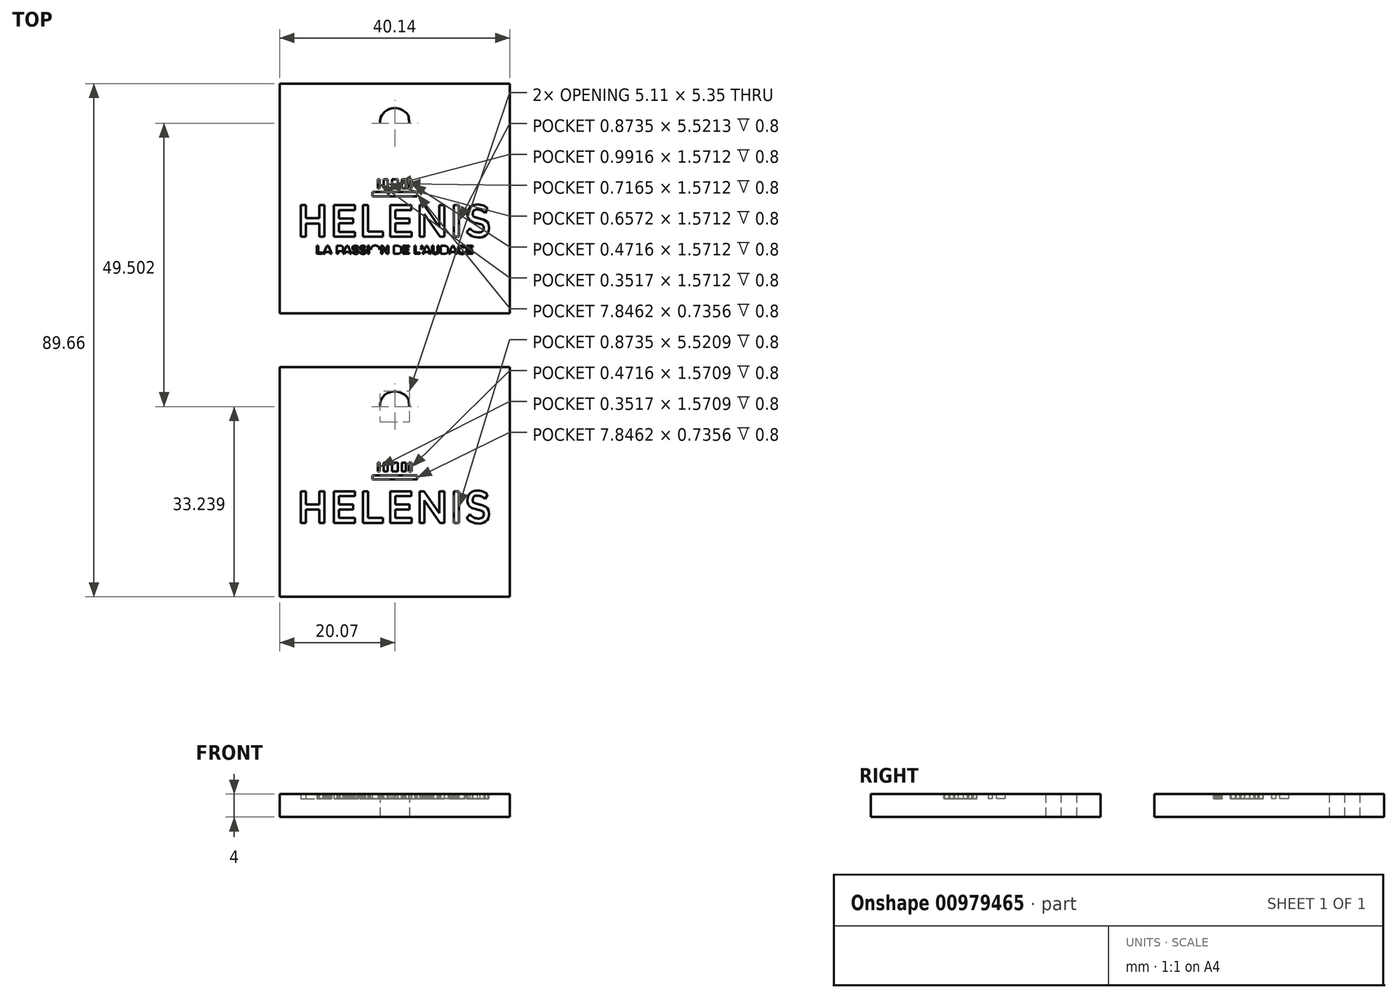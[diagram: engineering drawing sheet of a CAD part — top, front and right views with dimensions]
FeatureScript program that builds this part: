
annotation { "Feature Type Name" : "Feature", "Feature Type Description" : "" }
export const myFeature = defineFeature(function(context is Context, id is Id, definition is map)
    precondition{}
    {
        {
            var Q0;
            Q0=qCreatedBy(makeId("Top.planeOp"),FACE);
            var sketch = newSketch(context, id + "F0", { "sketchPlane" : qUnion([Q0])});
            skLineSegment(sketch, "E0", {"start": v(20.07, 44.83) * mm, "end": v(-20.07, 44.83) * mm});
            skLineSegment(sketch, "E1", {"start": v(-20.07, 44.83) * mm, "end": v(-20.07, 4.68) * mm});
            skLineSegment(sketch, "E2", {"start": v(-20.07, 4.68) * mm, "end": v(20.07, 4.68) * mm});
            skLineSegment(sketch, "E3", {"start": v(20.07, 4.68) * mm, "end": v(20.07, 44.83) * mm});
            skLineSegment(sketch, "E4", {"start": v(20.07, -4.68) * mm, "end": v(-20.07, -4.68) * mm});
            skLineSegment(sketch, "E5", {"start": v(-20.07, -4.68) * mm, "end": v(-20.07, -44.83) * mm});
            skLineSegment(sketch, "E6", {"start": v(-20.07, -44.83) * mm, "end": v(20.07, -44.83) * mm});
            skLineSegment(sketch, "E7", {"start": v(20.07, -44.83) * mm, "end": v(20.07, -4.68) * mm});
            skLineSegment(sketch, "E8", {"start": v(-13.6, 15.1) * mm, "end": v(-12.62, 15.1) * mm});
            skLineSegment(sketch, "E9", {"start": v(-12.62, 15.1) * mm, "end": v(-12.62, 15.33) * mm});
            skLineSegment(sketch, "E10", {"start": v(-12.62, 15.33) * mm, "end": v(-13.36, 15.33) * mm});
            skLineSegment(sketch, "E11", {"start": v(-13.36, 15.33) * mm, "end": v(-13.36, 16.5) * mm});
            skLineSegment(sketch, "E12", {"start": v(-13.36, 16.5) * mm, "end": v(-13.6, 16.5) * mm});
            skLineSegment(sketch, "E13", {"start": v(-13.6, 16.5) * mm, "end": v(-13.6, 15.1) * mm});
            skLineSegment(sketch, "E14", {"start": v(-11.62, 16.52) * mm, "end": v(-11.85, 16.52) * mm});
            skLineSegment(sketch, "E15", {"start": v(-11.85, 16.52) * mm, "end": v(-12.46, 15.1) * mm});
            skLineSegment(sketch, "E16", {"start": v(-12.46, 15.1) * mm, "end": v(-12.21, 15.1) * mm});
            skLineSegment(sketch, "E17", {"start": v(-12.21, 15.1) * mm, "end": v(-12.07, 15.44) * mm});
            skLineSegment(sketch, "E18", {"start": v(-12.07, 15.44) * mm, "end": v(-11.4, 15.44) * mm});
            skLineSegment(sketch, "E19", {"start": v(-11.4, 15.44) * mm, "end": v(-11.26, 15.1) * mm});
            skLineSegment(sketch, "E20", {"start": v(-11.26, 15.1) * mm, "end": v(-11, 15.1) * mm});
            skLineSegment(sketch, "E21", {"start": v(-11, 15.1) * mm, "end": v(-11.62, 16.52) * mm});
            skLineSegment(sketch, "E22", {"start": v(-11.5, 15.66) * mm, "end": v(-11.98, 15.66) * mm});
            skLineSegment(sketch, "E23", {"start": v(-11.98, 15.66) * mm, "end": v(-11.74, 16.22) * mm});
            skLineSegment(sketch, "E24", {"start": v(-11.74, 16.22) * mm, "end": v(-11.5, 15.66) * mm});
            skLineSegment(sketch, "E25", {"start": v(-9.57, 16.5) * mm, "end": v(-10.12, 16.5) * mm});
            skLineSegment(sketch, "E26", {"start": v(-10.12, 16.5) * mm, "end": v(-10.12, 15.1) * mm});
            skLineSegment(sketch, "E27", {"start": v(-10.12, 15.1) * mm, "end": v(-9.87, 15.1) * mm});
            skLineSegment(sketch, "E28", {"start": v(-9.87, 15.1) * mm, "end": v(-9.87, 15.56) * mm});
            skLineSegment(sketch, "E29", {"start": v(-9.87, 15.56) * mm, "end": v(-9.6, 15.56) * mm});
            skLineSegment(sketch, "E30", {"start": v(-9.59, 15.78) * mm, "end": v(-9.87, 15.78) * mm});
            skLineSegment(sketch, "E31", {"start": v(-9.87, 15.78) * mm, "end": v(-9.87, 16.28) * mm});
            skLineSegment(sketch, "E32", {"start": v(-9.87, 16.28) * mm, "end": v(-9.59, 16.28) * mm});
            skLineSegment(sketch, "E33", {"start": v(-8.18, 16.52) * mm, "end": v(-8.4, 16.52) * mm});
            skLineSegment(sketch, "E34", {"start": v(-8.4, 16.52) * mm, "end": v(-9.02, 15.1) * mm});
            skLineSegment(sketch, "E35", {"start": v(-9.02, 15.1) * mm, "end": v(-8.77, 15.1) * mm});
            skLineSegment(sketch, "E36", {"start": v(-8.77, 15.1) * mm, "end": v(-8.63, 15.44) * mm});
            skLineSegment(sketch, "E37", {"start": v(-8.63, 15.44) * mm, "end": v(-7.96, 15.44) * mm});
            skLineSegment(sketch, "E38", {"start": v(-7.96, 15.44) * mm, "end": v(-7.82, 15.1) * mm});
            skLineSegment(sketch, "E39", {"start": v(-7.82, 15.1) * mm, "end": v(-7.56, 15.1) * mm});
            skLineSegment(sketch, "E40", {"start": v(-7.56, 15.1) * mm, "end": v(-8.18, 16.52) * mm});
            skLineSegment(sketch, "E41", {"start": v(-8.05, 15.66) * mm, "end": v(-8.54, 15.66) * mm});
            skLineSegment(sketch, "E42", {"start": v(-8.54, 15.66) * mm, "end": v(-8.3, 16.22) * mm});
            skLineSegment(sketch, "E43", {"start": v(-8.3, 16.22) * mm, "end": v(-8.05, 15.66) * mm});
            skLineSegment(sketch, "E44", {"start": v(-6.5, 16.16) * mm, "end": v(-6.37, 16.35) * mm});
            skLineSegment(sketch, "E45", {"start": v(-7.27, 15.49) * mm, "end": v(-7.42, 15.3) * mm});
            skLineSegment(sketch, "E46", {"start": v(-5.23, 16.16) * mm, "end": v(-5.1, 16.35) * mm});
            skLineSegment(sketch, "E47", {"start": v(-5.99, 15.49) * mm, "end": v(-6.14, 15.3) * mm});
            skLineSegment(sketch, "E48", {"start": v(-4.73, 15.1) * mm, "end": v(-4.48, 15.1) * mm});
            skLineSegment(sketch, "E49", {"start": v(-4.48, 15.1) * mm, "end": v(-4.48, 16.5) * mm});
            skLineSegment(sketch, "E50", {"start": v(-4.48, 16.5) * mm, "end": v(-4.73, 16.5) * mm});
            skLineSegment(sketch, "E51", {"start": v(-4.73, 16.5) * mm, "end": v(-4.73, 15.1) * mm});
            skLineSegment(sketch, "E52", {"start": v(-1.39, 15.54) * mm, "end": v(-2.14, 16.5) * mm});
            skLineSegment(sketch, "E53", {"start": v(-2.14, 16.5) * mm, "end": v(-2.36, 16.5) * mm});
            skLineSegment(sketch, "E54", {"start": v(-2.36, 16.5) * mm, "end": v(-2.36, 15.1) * mm});
            skLineSegment(sketch, "E55", {"start": v(-2.36, 15.1) * mm, "end": v(-2.12, 15.1) * mm});
            skLineSegment(sketch, "E56", {"start": v(-2.12, 15.1) * mm, "end": v(-2.12, 16.1) * mm});
            skLineSegment(sketch, "E57", {"start": v(-2.12, 16.1) * mm, "end": v(-1.35, 15.1) * mm});
            skLineSegment(sketch, "E58", {"start": v(-1.35, 15.1) * mm, "end": v(-1.14, 15.1) * mm});
            skLineSegment(sketch, "E59", {"start": v(-1.14, 15.1) * mm, "end": v(-1.14, 16.5) * mm});
            skLineSegment(sketch, "E60", {"start": v(-1.14, 16.5) * mm, "end": v(-1.39, 16.5) * mm});
            skLineSegment(sketch, "E61", {"start": v(-1.39, 16.5) * mm, "end": v(-1.39, 15.54) * mm});
            skLineSegment(sketch, "E62", {"start": v(0.38, 16.5) * mm, "end": v(-0.14, 16.5) * mm});
            skLineSegment(sketch, "E63", {"start": v(-0.14, 16.5) * mm, "end": v(-0.14, 15.1) * mm});
            skLineSegment(sketch, "E64", {"start": v(-0.14, 15.1) * mm, "end": v(0.38, 15.1) * mm});
            skLineSegment(sketch, "E65", {"start": v(0.38, 15.33) * mm, "end": v(0.1, 15.33) * mm});
            skLineSegment(sketch, "E66", {"start": v(0.1, 15.33) * mm, "end": v(0.1, 16.28) * mm});
            skLineSegment(sketch, "E67", {"start": v(0.1, 16.28) * mm, "end": v(0.38, 16.28) * mm});
            skLineSegment(sketch, "E68", {"start": v(2.48, 16.5) * mm, "end": v(1.44, 16.5) * mm});
            skLineSegment(sketch, "E69", {"start": v(1.44, 16.5) * mm, "end": v(1.44, 15.1) * mm});
            skLineSegment(sketch, "E70", {"start": v(1.44, 15.1) * mm, "end": v(2.5, 15.1) * mm});
            skLineSegment(sketch, "E71", {"start": v(2.5, 15.1) * mm, "end": v(2.5, 15.33) * mm});
            skLineSegment(sketch, "E72", {"start": v(2.5, 15.33) * mm, "end": v(1.7, 15.33) * mm});
            skLineSegment(sketch, "E73", {"start": v(1.7, 15.33) * mm, "end": v(1.7, 15.7) * mm});
            skLineSegment(sketch, "E74", {"start": v(1.7, 15.7) * mm, "end": v(2.4, 15.7) * mm});
            skLineSegment(sketch, "E75", {"start": v(2.4, 15.7) * mm, "end": v(2.4, 15.92) * mm});
            skLineSegment(sketch, "E76", {"start": v(2.4, 15.92) * mm, "end": v(1.7, 15.92) * mm});
            skLineSegment(sketch, "E77", {"start": v(1.7, 15.92) * mm, "end": v(1.7, 16.29) * mm});
            skLineSegment(sketch, "E78", {"start": v(1.7, 16.29) * mm, "end": v(2.48, 16.29) * mm});
            skLineSegment(sketch, "E79", {"start": v(2.48, 16.29) * mm, "end": v(2.48, 16.5) * mm});
            skLineSegment(sketch, "E80", {"start": v(3.43, 15.1) * mm, "end": v(4.4, 15.1) * mm});
            skLineSegment(sketch, "E81", {"start": v(4.4, 15.1) * mm, "end": v(4.4, 15.33) * mm});
            skLineSegment(sketch, "E82", {"start": v(4.4, 15.33) * mm, "end": v(3.67, 15.33) * mm});
            skLineSegment(sketch, "E83", {"start": v(3.67, 15.33) * mm, "end": v(3.67, 16.5) * mm});
            skLineSegment(sketch, "E84", {"start": v(3.67, 16.5) * mm, "end": v(3.43, 16.5) * mm});
            skLineSegment(sketch, "E85", {"start": v(3.43, 16.5) * mm, "end": v(3.43, 15.1) * mm});
            skLineSegment(sketch, "E86", {"start": v(4.5, 16.04) * mm, "end": v(4.53, 15.94) * mm});
            skLineSegment(sketch, "E87", {"start": v(4.84, 16.27) * mm, "end": v(4.84, 16.5) * mm});
            skLineSegment(sketch, "E88", {"start": v(4.84, 16.5) * mm, "end": v(4.57, 16.5) * mm});
            skLineSegment(sketch, "E89", {"start": v(4.57, 16.5) * mm, "end": v(4.57, 16.23) * mm});
            skLineSegment(sketch, "E90", {"start": v(4.57, 16.23) * mm, "end": v(4.67, 16.23) * mm});
            skLineSegment(sketch, "E91", {"start": v(5.69, 16.52) * mm, "end": v(5.46, 16.52) * mm});
            skLineSegment(sketch, "E92", {"start": v(5.46, 16.52) * mm, "end": v(4.84, 15.1) * mm});
            skLineSegment(sketch, "E93", {"start": v(4.84, 15.1) * mm, "end": v(5.1, 15.1) * mm});
            skLineSegment(sketch, "E94", {"start": v(5.1, 15.1) * mm, "end": v(5.24, 15.44) * mm});
            skLineSegment(sketch, "E95", {"start": v(5.24, 15.44) * mm, "end": v(5.9, 15.44) * mm});
            skLineSegment(sketch, "E96", {"start": v(5.9, 15.44) * mm, "end": v(6.04, 15.1) * mm});
            skLineSegment(sketch, "E97", {"start": v(6.04, 15.1) * mm, "end": v(6.3, 15.1) * mm});
            skLineSegment(sketch, "E98", {"start": v(6.3, 15.1) * mm, "end": v(5.69, 16.52) * mm});
            skLineSegment(sketch, "E99", {"start": v(5.81, 15.66) * mm, "end": v(5.33, 15.66) * mm});
            skLineSegment(sketch, "E100", {"start": v(5.33, 15.66) * mm, "end": v(5.57, 16.22) * mm});
            skLineSegment(sketch, "E101", {"start": v(5.57, 16.22) * mm, "end": v(5.81, 15.66) * mm});
            skLineSegment(sketch, "E102", {"start": v(7.7, 16.5) * mm, "end": v(7.45, 16.5) * mm});
            skLineSegment(sketch, "E103", {"start": v(7.45, 16.5) * mm, "end": v(7.45, 15.7) * mm});
            skLineSegment(sketch, "E104", {"start": v(6.74, 15.7) * mm, "end": v(6.74, 16.5) * mm});
            skLineSegment(sketch, "E105", {"start": v(6.74, 16.5) * mm, "end": v(6.5, 16.5) * mm});
            skLineSegment(sketch, "E106", {"start": v(6.5, 16.5) * mm, "end": v(6.5, 15.7) * mm});
            skLineSegment(sketch, "E107", {"start": v(7.7, 15.71) * mm, "end": v(7.7, 16.5) * mm});
            skLineSegment(sketch, "E108", {"start": v(8.57, 16.5) * mm, "end": v(8.05, 16.5) * mm});
            skLineSegment(sketch, "E109", {"start": v(8.05, 16.5) * mm, "end": v(8.05, 15.1) * mm});
            skLineSegment(sketch, "E110", {"start": v(8.05, 15.1) * mm, "end": v(8.57, 15.1) * mm});
            skLineSegment(sketch, "E111", {"start": v(8.57, 15.33) * mm, "end": v(8.3, 15.33) * mm});
            skLineSegment(sketch, "E112", {"start": v(8.3, 15.33) * mm, "end": v(8.3, 16.28) * mm});
            skLineSegment(sketch, "E113", {"start": v(8.3, 16.28) * mm, "end": v(8.57, 16.28) * mm});
            skLineSegment(sketch, "E114", {"start": v(10.26, 16.52) * mm, "end": v(10.04, 16.52) * mm});
            skLineSegment(sketch, "E115", {"start": v(10.04, 16.52) * mm, "end": v(9.42, 15.1) * mm});
            skLineSegment(sketch, "E116", {"start": v(9.42, 15.1) * mm, "end": v(9.67, 15.1) * mm});
            skLineSegment(sketch, "E117", {"start": v(9.67, 15.1) * mm, "end": v(9.82, 15.44) * mm});
            skLineSegment(sketch, "E118", {"start": v(9.82, 15.44) * mm, "end": v(10.48, 15.44) * mm});
            skLineSegment(sketch, "E119", {"start": v(10.48, 15.44) * mm, "end": v(10.62, 15.1) * mm});
            skLineSegment(sketch, "E120", {"start": v(10.62, 15.1) * mm, "end": v(10.88, 15.1) * mm});
            skLineSegment(sketch, "E121", {"start": v(10.88, 15.1) * mm, "end": v(10.26, 16.52) * mm});
            skLineSegment(sketch, "E122", {"start": v(10.39, 15.66) * mm, "end": v(9.9, 15.66) * mm});
            skLineSegment(sketch, "E123", {"start": v(9.9, 15.66) * mm, "end": v(10.15, 16.22) * mm});
            skLineSegment(sketch, "E124", {"start": v(10.15, 16.22) * mm, "end": v(10.39, 15.66) * mm});
            skLineSegment(sketch, "E125", {"start": v(12.27, 15.33) * mm, "end": v(12.12, 15.49) * mm});
            skLineSegment(sketch, "E126", {"start": v(12.1, 16.13) * mm, "end": v(12.26, 16.31) * mm});
            skLineSegment(sketch, "E127", {"start": v(13.6, 16.5) * mm, "end": v(12.55, 16.5) * mm});
            skLineSegment(sketch, "E128", {"start": v(12.55, 16.5) * mm, "end": v(12.55, 15.1) * mm});
            skLineSegment(sketch, "E129", {"start": v(12.55, 15.1) * mm, "end": v(13.6, 15.1) * mm});
            skLineSegment(sketch, "E130", {"start": v(13.6, 15.1) * mm, "end": v(13.6, 15.33) * mm});
            skLineSegment(sketch, "E131", {"start": v(13.6, 15.33) * mm, "end": v(12.8, 15.33) * mm});
            skLineSegment(sketch, "E132", {"start": v(12.8, 15.33) * mm, "end": v(12.8, 15.7) * mm});
            skLineSegment(sketch, "E133", {"start": v(12.8, 15.7) * mm, "end": v(13.5, 15.7) * mm});
            skLineSegment(sketch, "E134", {"start": v(13.5, 15.7) * mm, "end": v(13.5, 15.92) * mm});
            skLineSegment(sketch, "E135", {"start": v(13.5, 15.92) * mm, "end": v(12.8, 15.92) * mm});
            skLineSegment(sketch, "E136", {"start": v(12.8, 15.92) * mm, "end": v(12.8, 16.29) * mm});
            skLineSegment(sketch, "E137", {"start": v(12.8, 16.29) * mm, "end": v(13.6, 16.29) * mm});
            skLineSegment(sketch, "E138", {"start": v(13.6, 16.29) * mm, "end": v(13.6, 16.5) * mm});
            skLineSegment(sketch, "E139", {"start": v(-3.92, 25.17) * mm, "end": v(3.92, 25.17) * mm});
            skLineSegment(sketch, "E140", {"start": v(3.92, 25.17) * mm, "end": v(3.92, 25.9) * mm});
            skLineSegment(sketch, "E141", {"start": v(3.92, 25.9) * mm, "end": v(-3.92, 25.9) * mm});
            skLineSegment(sketch, "E142", {"start": v(-3.92, 25.9) * mm, "end": v(-3.92, 25.17) * mm});
            skLineSegment(sketch, "E143", {"start": v(-2.97, 26.56) * mm, "end": v(-2.62, 26.56) * mm});
            skLineSegment(sketch, "E144", {"start": v(-2.62, 26.56) * mm, "end": v(-2.62, 28.13) * mm});
            skLineSegment(sketch, "E145", {"start": v(-2.62, 28.13) * mm, "end": v(-2.97, 28.13) * mm});
            skLineSegment(sketch, "E146", {"start": v(-2.97, 28.13) * mm, "end": v(-2.97, 26.56) * mm});
            skLineSegment(sketch, "E147", {"start": v(2.47, 26.56) * mm, "end": v(2.94, 26.56) * mm});
            skLineSegment(sketch, "E148", {"start": v(2.94, 26.56) * mm, "end": v(2.94, 28.13) * mm});
            skLineSegment(sketch, "E149", {"start": v(2.94, 28.13) * mm, "end": v(2.47, 28.13) * mm});
            skLineSegment(sketch, "E150", {"start": v(2.47, 28.13) * mm, "end": v(2.47, 26.56) * mm});
            skLineSegment(sketch, "E151", {"start": v(-1.93, 26.56) * mm, "end": v(-1.27, 26.56) * mm});
            skLineSegment(sketch, "E152", {"start": v(-1.27, 26.56) * mm, "end": v(-1.27, 28.13) * mm});
            skLineSegment(sketch, "E153", {"start": v(-1.27, 28.13) * mm, "end": v(-1.93, 28.13) * mm});
            skLineSegment(sketch, "E154", {"start": v(-1.93, 28.13) * mm, "end": v(-1.93, 26.56) * mm});
            skLineSegment(sketch, "E155", {"start": v(1.23, 26.56) * mm, "end": v(1.95, 26.56) * mm});
            skLineSegment(sketch, "E156", {"start": v(1.95, 26.56) * mm, "end": v(1.95, 28.13) * mm});
            skLineSegment(sketch, "E157", {"start": v(1.95, 28.13) * mm, "end": v(1.23, 28.13) * mm});
            skLineSegment(sketch, "E158", {"start": v(1.23, 28.13) * mm, "end": v(1.23, 26.56) * mm});
            skLineSegment(sketch, "E159", {"start": v(-0.47, 26.56) * mm, "end": v(0.52, 26.56) * mm});
            skLineSegment(sketch, "E160", {"start": v(0.52, 26.56) * mm, "end": v(0.52, 28.13) * mm});
            skLineSegment(sketch, "E161", {"start": v(0.52, 28.13) * mm, "end": v(-0.47, 28.13) * mm});
            skLineSegment(sketch, "E162", {"start": v(-0.47, 28.13) * mm, "end": v(-0.47, 26.56) * mm});
            skLineSegment(sketch, "E163", {"start": v(-13.16, 20.41) * mm, "end": v(-13.16, 18.09) * mm});
            skLineSegment(sketch, "E164", {"start": v(-13.16, 18.09) * mm, "end": v(-12.28, 18.09) * mm});
            skLineSegment(sketch, "E165", {"start": v(-12.28, 18.09) * mm, "end": v(-12.28, 23.6) * mm});
            skLineSegment(sketch, "E166", {"start": v(-12.28, 23.6) * mm, "end": v(-13.16, 23.6) * mm});
            skLineSegment(sketch, "E167", {"start": v(-13.16, 23.6) * mm, "end": v(-13.16, 21.31) * mm});
            skLineSegment(sketch, "E168", {"start": v(-13.16, 21.31) * mm, "end": v(-15.53, 21.31) * mm});
            skLineSegment(sketch, "E169", {"start": v(-15.53, 21.31) * mm, "end": v(-15.53, 23.6) * mm});
            skLineSegment(sketch, "E170", {"start": v(-15.53, 23.6) * mm, "end": v(-16.4, 23.6) * mm});
            skLineSegment(sketch, "E171", {"start": v(-16.4, 23.6) * mm, "end": v(-16.4, 18.09) * mm});
            skLineSegment(sketch, "E172", {"start": v(-16.4, 18.09) * mm, "end": v(-15.53, 18.09) * mm});
            skLineSegment(sketch, "E173", {"start": v(-15.53, 18.09) * mm, "end": v(-15.53, 20.41) * mm});
            skLineSegment(sketch, "E174", {"start": v(-15.53, 20.41) * mm, "end": v(-13.16, 20.41) * mm});
            skLineSegment(sketch, "E175", {"start": v(-6.97, 23.6) * mm, "end": v(-10.65, 23.6) * mm});
            skLineSegment(sketch, "E176", {"start": v(-10.65, 23.6) * mm, "end": v(-10.65, 18.09) * mm});
            skLineSegment(sketch, "E177", {"start": v(-10.65, 18.09) * mm, "end": v(-6.93, 18.09) * mm});
            skLineSegment(sketch, "E178", {"start": v(-6.93, 18.09) * mm, "end": v(-6.93, 18.96) * mm});
            skLineSegment(sketch, "E179", {"start": v(-6.93, 18.96) * mm, "end": v(-9.78, 18.96) * mm});
            skLineSegment(sketch, "E180", {"start": v(-9.78, 18.96) * mm, "end": v(-9.78, 20.44) * mm});
            skLineSegment(sketch, "E181", {"start": v(-9.78, 20.44) * mm, "end": v(-7.29, 20.44) * mm});
            skLineSegment(sketch, "E182", {"start": v(-7.29, 20.44) * mm, "end": v(-7.29, 21.3) * mm});
            skLineSegment(sketch, "E183", {"start": v(-7.29, 21.3) * mm, "end": v(-9.78, 21.3) * mm});
            skLineSegment(sketch, "E184", {"start": v(-9.78, 21.3) * mm, "end": v(-9.78, 22.74) * mm});
            skLineSegment(sketch, "E185", {"start": v(-9.78, 22.74) * mm, "end": v(-6.97, 22.74) * mm});
            skLineSegment(sketch, "E186", {"start": v(-6.97, 22.74) * mm, "end": v(-6.97, 23.6) * mm});
            skLineSegment(sketch, "E187", {"start": v(-5.54, 18.09) * mm, "end": v(-2.05, 18.09) * mm});
            skLineSegment(sketch, "E188", {"start": v(-2.05, 18.09) * mm, "end": v(-2.05, 18.97) * mm});
            skLineSegment(sketch, "E189", {"start": v(-2.05, 18.97) * mm, "end": v(-4.67, 18.97) * mm});
            skLineSegment(sketch, "E190", {"start": v(-4.67, 18.97) * mm, "end": v(-4.67, 23.6) * mm});
            skLineSegment(sketch, "E191", {"start": v(-4.67, 23.6) * mm, "end": v(-5.54, 23.6) * mm});
            skLineSegment(sketch, "E192", {"start": v(-5.54, 23.6) * mm, "end": v(-5.54, 18.09) * mm});
            skLineSegment(sketch, "E193", {"start": v(2.9, 23.6) * mm, "end": v(-0.8, 23.6) * mm});
            skLineSegment(sketch, "E194", {"start": v(-0.8, 23.6) * mm, "end": v(-0.8, 18.09) * mm});
            skLineSegment(sketch, "E195", {"start": v(-0.8, 18.09) * mm, "end": v(2.93, 18.09) * mm});
            skLineSegment(sketch, "E196", {"start": v(2.93, 18.09) * mm, "end": v(2.93, 18.96) * mm});
            skLineSegment(sketch, "E197", {"start": v(2.93, 18.96) * mm, "end": v(0.08, 18.96) * mm});
            skLineSegment(sketch, "E198", {"start": v(0.08, 18.96) * mm, "end": v(0.08, 20.44) * mm});
            skLineSegment(sketch, "E199", {"start": v(0.08, 20.44) * mm, "end": v(2.57, 20.44) * mm});
            skLineSegment(sketch, "E200", {"start": v(2.57, 20.44) * mm, "end": v(2.57, 21.3) * mm});
            skLineSegment(sketch, "E201", {"start": v(2.57, 21.3) * mm, "end": v(0.08, 21.3) * mm});
            skLineSegment(sketch, "E202", {"start": v(0.08, 21.3) * mm, "end": v(0.08, 22.74) * mm});
            skLineSegment(sketch, "E203", {"start": v(0.08, 22.74) * mm, "end": v(2.9, 22.74) * mm});
            skLineSegment(sketch, "E204", {"start": v(2.9, 22.74) * mm, "end": v(2.9, 23.6) * mm});
            skLineSegment(sketch, "E205", {"start": v(7.8, 19.8) * mm, "end": v(5.13, 23.6) * mm});
            skLineSegment(sketch, "E206", {"start": v(5.13, 23.6) * mm, "end": v(4.32, 23.6) * mm});
            skLineSegment(sketch, "E207", {"start": v(4.32, 23.6) * mm, "end": v(4.32, 18.09) * mm});
            skLineSegment(sketch, "E208", {"start": v(4.32, 18.09) * mm, "end": v(5.18, 18.09) * mm});
            skLineSegment(sketch, "E209", {"start": v(5.18, 18.09) * mm, "end": v(5.18, 22.02) * mm});
            skLineSegment(sketch, "E210", {"start": v(5.18, 22.02) * mm, "end": v(7.92, 18.09) * mm});
            skLineSegment(sketch, "E211", {"start": v(7.92, 18.09) * mm, "end": v(8.65, 18.09) * mm});
            skLineSegment(sketch, "E212", {"start": v(8.65, 18.09) * mm, "end": v(8.65, 23.6) * mm});
            skLineSegment(sketch, "E213", {"start": v(8.65, 23.6) * mm, "end": v(7.8, 23.6) * mm});
            skLineSegment(sketch, "E214", {"start": v(7.8, 23.6) * mm, "end": v(7.8, 19.8) * mm});
            skLineSegment(sketch, "E215", {"start": v(10.33, 18.09) * mm, "end": v(11.2, 18.09) * mm});
            skLineSegment(sketch, "E216", {"start": v(11.2, 18.09) * mm, "end": v(11.2, 23.6) * mm});
            skLineSegment(sketch, "E217", {"start": v(11.2, 23.6) * mm, "end": v(10.33, 23.6) * mm});
            skLineSegment(sketch, "E218", {"start": v(10.33, 23.6) * mm, "end": v(10.33, 18.09) * mm});
            skLineSegment(sketch, "E219", {"start": v(15.78, 22.26) * mm, "end": v(16.25, 23) * mm});
            skLineSegment(sketch, "E220", {"start": v(13.08, 19.59) * mm, "end": v(12.55, 18.9) * mm});
            skLineSegment(sketch, "E221", {"start": v(-3.92, -24.34) * mm, "end": v(3.92, -24.34) * mm});
            skLineSegment(sketch, "E222", {"start": v(3.92, -24.34) * mm, "end": v(3.92, -23.6) * mm});
            skLineSegment(sketch, "E223", {"start": v(3.92, -23.6) * mm, "end": v(-3.92, -23.6) * mm});
            skLineSegment(sketch, "E224", {"start": v(-3.92, -23.6) * mm, "end": v(-3.92, -24.34) * mm});
            skLineSegment(sketch, "E225", {"start": v(-2.97, -22.94) * mm, "end": v(-2.62, -22.94) * mm});
            skLineSegment(sketch, "E226", {"start": v(-2.62, -22.94) * mm, "end": v(-2.62, -21.37) * mm});
            skLineSegment(sketch, "E227", {"start": v(-2.62, -21.37) * mm, "end": v(-2.97, -21.37) * mm});
            skLineSegment(sketch, "E228", {"start": v(-2.97, -21.37) * mm, "end": v(-2.97, -22.94) * mm});
            skLineSegment(sketch, "E229", {"start": v(2.47, -22.94) * mm, "end": v(2.94, -22.94) * mm});
            skLineSegment(sketch, "E230", {"start": v(2.94, -22.94) * mm, "end": v(2.94, -21.37) * mm});
            skLineSegment(sketch, "E231", {"start": v(2.94, -21.37) * mm, "end": v(2.47, -21.37) * mm});
            skLineSegment(sketch, "E232", {"start": v(2.47, -21.37) * mm, "end": v(2.47, -22.94) * mm});
            skLineSegment(sketch, "E233", {"start": v(-1.93, -22.94) * mm, "end": v(-1.27, -22.94) * mm});
            skLineSegment(sketch, "E234", {"start": v(-1.27, -22.94) * mm, "end": v(-1.27, -21.37) * mm});
            skLineSegment(sketch, "E235", {"start": v(-1.27, -21.37) * mm, "end": v(-1.93, -21.37) * mm});
            skLineSegment(sketch, "E236", {"start": v(-1.93, -21.37) * mm, "end": v(-1.93, -22.94) * mm});
            skLineSegment(sketch, "E237", {"start": v(1.23, -22.94) * mm, "end": v(1.95, -22.94) * mm});
            skLineSegment(sketch, "E238", {"start": v(1.95, -22.94) * mm, "end": v(1.95, -21.37) * mm});
            skLineSegment(sketch, "E239", {"start": v(1.95, -21.37) * mm, "end": v(1.23, -21.37) * mm});
            skLineSegment(sketch, "E240", {"start": v(1.23, -21.37) * mm, "end": v(1.23, -22.94) * mm});
            skLineSegment(sketch, "E241", {"start": v(-0.47, -22.94) * mm, "end": v(0.52, -22.94) * mm});
            skLineSegment(sketch, "E242", {"start": v(0.52, -22.94) * mm, "end": v(0.52, -21.37) * mm});
            skLineSegment(sketch, "E243", {"start": v(0.52, -21.37) * mm, "end": v(-0.47, -21.37) * mm});
            skLineSegment(sketch, "E244", {"start": v(-0.47, -21.37) * mm, "end": v(-0.47, -22.94) * mm});
            skLineSegment(sketch, "E245", {"start": v(-13.16, -29.59) * mm, "end": v(-13.16, -31.92) * mm});
            skLineSegment(sketch, "E246", {"start": v(-13.16, -31.92) * mm, "end": v(-12.28, -31.92) * mm});
            skLineSegment(sketch, "E247", {"start": v(-12.28, -31.92) * mm, "end": v(-12.28, -26.4) * mm});
            skLineSegment(sketch, "E248", {"start": v(-12.28, -26.4) * mm, "end": v(-13.16, -26.4) * mm});
            skLineSegment(sketch, "E249", {"start": v(-13.16, -26.4) * mm, "end": v(-13.16, -28.69) * mm});
            skLineSegment(sketch, "E250", {"start": v(-13.16, -28.69) * mm, "end": v(-15.53, -28.69) * mm});
            skLineSegment(sketch, "E251", {"start": v(-15.53, -28.69) * mm, "end": v(-15.53, -26.4) * mm});
            skLineSegment(sketch, "E252", {"start": v(-15.53, -26.4) * mm, "end": v(-16.4, -26.4) * mm});
            skLineSegment(sketch, "E253", {"start": v(-16.4, -26.4) * mm, "end": v(-16.4, -31.92) * mm});
            skLineSegment(sketch, "E254", {"start": v(-16.4, -31.92) * mm, "end": v(-15.53, -31.92) * mm});
            skLineSegment(sketch, "E255", {"start": v(-15.53, -31.92) * mm, "end": v(-15.53, -29.59) * mm});
            skLineSegment(sketch, "E256", {"start": v(-15.53, -29.59) * mm, "end": v(-13.16, -29.59) * mm});
            skLineSegment(sketch, "E257", {"start": v(-6.97, -26.4) * mm, "end": v(-10.65, -26.4) * mm});
            skLineSegment(sketch, "E258", {"start": v(-10.65, -26.4) * mm, "end": v(-10.65, -31.92) * mm});
            skLineSegment(sketch, "E259", {"start": v(-10.65, -31.92) * mm, "end": v(-6.93, -31.92) * mm});
            skLineSegment(sketch, "E260", {"start": v(-6.93, -31.92) * mm, "end": v(-6.93, -31.05) * mm});
            skLineSegment(sketch, "E261", {"start": v(-6.93, -31.05) * mm, "end": v(-9.78, -31.05) * mm});
            skLineSegment(sketch, "E262", {"start": v(-9.78, -31.05) * mm, "end": v(-9.78, -29.56) * mm});
            skLineSegment(sketch, "E263", {"start": v(-9.78, -29.56) * mm, "end": v(-7.29, -29.56) * mm});
            skLineSegment(sketch, "E264", {"start": v(-7.29, -29.56) * mm, "end": v(-7.29, -28.7) * mm});
            skLineSegment(sketch, "E265", {"start": v(-7.29, -28.7) * mm, "end": v(-9.78, -28.7) * mm});
            skLineSegment(sketch, "E266", {"start": v(-9.78, -28.7) * mm, "end": v(-9.78, -27.26) * mm});
            skLineSegment(sketch, "E267", {"start": v(-9.78, -27.26) * mm, "end": v(-6.97, -27.26) * mm});
            skLineSegment(sketch, "E268", {"start": v(-6.97, -27.26) * mm, "end": v(-6.97, -26.4) * mm});
            skLineSegment(sketch, "E269", {"start": v(-5.54, -31.92) * mm, "end": v(-2.05, -31.92) * mm});
            skLineSegment(sketch, "E270", {"start": v(-2.05, -31.92) * mm, "end": v(-2.05, -31.03) * mm});
            skLineSegment(sketch, "E271", {"start": v(-2.05, -31.03) * mm, "end": v(-4.67, -31.03) * mm});
            skLineSegment(sketch, "E272", {"start": v(-4.67, -31.03) * mm, "end": v(-4.67, -26.4) * mm});
            skLineSegment(sketch, "E273", {"start": v(-4.67, -26.4) * mm, "end": v(-5.54, -26.4) * mm});
            skLineSegment(sketch, "E274", {"start": v(-5.54, -26.4) * mm, "end": v(-5.54, -31.92) * mm});
            skLineSegment(sketch, "E275", {"start": v(2.9, -26.4) * mm, "end": v(-0.8, -26.4) * mm});
            skLineSegment(sketch, "E276", {"start": v(-0.8, -26.4) * mm, "end": v(-0.8, -31.92) * mm});
            skLineSegment(sketch, "E277", {"start": v(-0.8, -31.92) * mm, "end": v(2.93, -31.92) * mm});
            skLineSegment(sketch, "E278", {"start": v(2.93, -31.92) * mm, "end": v(2.93, -31.05) * mm});
            skLineSegment(sketch, "E279", {"start": v(2.93, -31.05) * mm, "end": v(0.08, -31.05) * mm});
            skLineSegment(sketch, "E280", {"start": v(0.08, -31.05) * mm, "end": v(0.08, -29.56) * mm});
            skLineSegment(sketch, "E281", {"start": v(0.08, -29.56) * mm, "end": v(2.57, -29.56) * mm});
            skLineSegment(sketch, "E282", {"start": v(2.57, -29.56) * mm, "end": v(2.57, -28.7) * mm});
            skLineSegment(sketch, "E283", {"start": v(2.57, -28.7) * mm, "end": v(0.08, -28.7) * mm});
            skLineSegment(sketch, "E284", {"start": v(0.08, -28.7) * mm, "end": v(0.08, -27.26) * mm});
            skLineSegment(sketch, "E285", {"start": v(0.08, -27.26) * mm, "end": v(2.9, -27.26) * mm});
            skLineSegment(sketch, "E286", {"start": v(2.9, -27.26) * mm, "end": v(2.9, -26.4) * mm});
            skLineSegment(sketch, "E287", {"start": v(7.8, -30.21) * mm, "end": v(5.13, -26.4) * mm});
            skLineSegment(sketch, "E288", {"start": v(5.13, -26.4) * mm, "end": v(4.32, -26.4) * mm});
            skLineSegment(sketch, "E289", {"start": v(4.32, -26.4) * mm, "end": v(4.32, -31.92) * mm});
            skLineSegment(sketch, "E290", {"start": v(4.32, -31.92) * mm, "end": v(5.18, -31.92) * mm});
            skLineSegment(sketch, "E291", {"start": v(5.18, -31.92) * mm, "end": v(5.18, -27.99) * mm});
            skLineSegment(sketch, "E292", {"start": v(5.18, -27.99) * mm, "end": v(7.92, -31.92) * mm});
            skLineSegment(sketch, "E293", {"start": v(7.92, -31.92) * mm, "end": v(8.65, -31.92) * mm});
            skLineSegment(sketch, "E294", {"start": v(8.65, -31.92) * mm, "end": v(8.65, -26.4) * mm});
            skLineSegment(sketch, "E295", {"start": v(8.65, -26.4) * mm, "end": v(7.8, -26.4) * mm});
            skLineSegment(sketch, "E296", {"start": v(7.8, -26.4) * mm, "end": v(7.8, -30.21) * mm});
            skLineSegment(sketch, "E297", {"start": v(10.33, -31.92) * mm, "end": v(11.2, -31.92) * mm});
            skLineSegment(sketch, "E298", {"start": v(11.2, -31.92) * mm, "end": v(11.2, -26.4) * mm});
            skLineSegment(sketch, "E299", {"start": v(11.2, -26.4) * mm, "end": v(10.33, -26.4) * mm});
            skLineSegment(sketch, "E300", {"start": v(10.33, -26.4) * mm, "end": v(10.33, -31.92) * mm});
            skLineSegment(sketch, "E301", {"start": v(15.78, -27.74) * mm, "end": v(16.25, -27) * mm});
            skLineSegment(sketch, "E302", {"start": v(13.08, -30.42) * mm, "end": v(12.55, -31.11) * mm});
            skFitSpline(sketch, "E303", {"points": [v(2.55, 37.91) * mm, v(2.48, 37.46) * mm, v(2.35, 36.57) * mm, v(1.33, 35.6) * mm, v(0, 35.23) * mm, v(-1.34, 35.6) * mm, v(-2.31, 36.57) * mm, v(-2.55, 37.46) * mm, v(-2.55, 37.91) * mm]});
            skFitSpline(sketch, "E304", {"points": [v(-2.55, 37.91) * mm, v(-2.55, 37.91) * mm, v(-2.56, 38.36) * mm, v(-2.31, 39.25) * mm, v(-1.34, 40.23) * mm, v(0, 40.59) * mm, v(1.33, 40.23) * mm, v(2.35, 39.25) * mm, v(2.48, 38.36) * mm, v(2.55, 37.91) * mm]});
            skFitSpline(sketch, "E305", {"points": [v(2.55, -11.6) * mm, v(2.48, -12.04) * mm, v(2.35, -12.93) * mm, v(1.33, -13.9) * mm, v(0, -14.27) * mm, v(-1.34, -13.9) * mm, v(-2.31, -12.93) * mm, v(-2.56, -12.04) * mm, v(-2.55, -11.6) * mm, v(-2.55, -11.6) * mm]});
            skFitSpline(sketch, "E306", {"points": [v(-2.55, -11.6) * mm, v(-2.55, -11.14) * mm, v(-2.31, -10.25) * mm, v(-1.34, -9.28) * mm, v(0, -8.91) * mm, v(1.33, -9.28) * mm, v(2.35, -10.25) * mm, v(2.48, -11.14) * mm, v(2.55, -11.6) * mm]});
            skFitSpline(sketch, "E307", {"points": [v(-9.03, 16.04) * mm, v(-9.05, 16.12) * mm, v(-9.07, 16.3) * mm, v(-9.29, 16.48) * mm, v(-9.47, 16.5) * mm, v(-9.57, 16.5) * mm]});
            skFitSpline(sketch, "E308", {"points": [v(-9.6, 15.56) * mm, v(-9.5, 15.56) * mm, v(-9.32, 15.58) * mm, v(-9.08, 15.76) * mm, v(-9.05, 15.94) * mm, v(-9.03, 16.04) * mm]});
            skFitSpline(sketch, "E309", {"points": [v(-9.29, 16.03) * mm, v(-9.3, 15.98) * mm, v(-9.3, 15.9) * mm, v(-9.43, 15.8) * mm, v(-9.53, 15.78) * mm, v(-9.59, 15.78) * mm]});
            skFitSpline(sketch, "E310", {"points": [v(-9.59, 16.28) * mm, v(-9.53, 16.28) * mm, v(-9.43, 16.27) * mm, v(-9.3, 16.18) * mm, v(-9.3, 16.08) * mm, v(-9.29, 16.03) * mm]});
            skFitSpline(sketch, "E311", {"points": [v(-7.11, 16.14) * mm, v(-7.1, 16.17) * mm, v(-7.1, 16.23) * mm, v(-7, 16.3) * mm, v(-6.89, 16.31) * mm, v(-6.76, 16.3) * mm, v(-6.63, 16.25) * mm, v(-6.55, 16.2) * mm, v(-6.5, 16.16) * mm]});
            skFitSpline(sketch, "E312", {"points": [v(-6.37, 16.35) * mm, v(-6.42, 16.39) * mm, v(-6.52, 16.45) * mm, v(-6.7, 16.51) * mm, v(-6.9, 16.54) * mm, v(-7.13, 16.5) * mm, v(-7.32, 16.34) * mm, v(-7.38, 16.12) * mm, v(-7.33, 15.9) * mm, v(-7.13, 15.76) * mm, v(-6.91, 15.7) * mm, v(-6.72, 15.66) * mm, v(-6.6, 15.59) * mm, v(-6.57, 15.48) * mm, v(-6.6, 15.38) * mm, v(-6.7, 15.31) * mm, v(-6.84, 15.3) * mm, v(-6.99, 15.32) * mm, v(-7.14, 15.38) * mm, v(-7.23, 15.45) * mm, v(-7.27, 15.49) * mm]});
            skFitSpline(sketch, "E313", {"points": [v(-7.42, 15.3) * mm, v(-7.36, 15.26) * mm, v(-7.25, 15.18) * mm, v(-7.04, 15.1) * mm, v(-6.82, 15.07) * mm, v(-6.58, 15.1) * mm, v(-6.37, 15.27) * mm, v(-6.31, 15.5) * mm, v(-6.36, 15.71) * mm, v(-6.55, 15.86) * mm, v(-6.77, 15.92) * mm, v(-6.96, 15.96) * mm, v(-7.1, 16.03) * mm, v(-7.1, 16.1) * mm, v(-7.11, 16.14) * mm]});
            skFitSpline(sketch, "E314", {"points": [v(-5.83, 16.14) * mm, v(-5.83, 16.17) * mm, v(-5.82, 16.23) * mm, v(-5.72, 16.3) * mm, v(-5.6, 16.31) * mm, v(-5.47, 16.3) * mm, v(-5.34, 16.25) * mm, v(-5.27, 16.2) * mm, v(-5.23, 16.16) * mm]});
            skFitSpline(sketch, "E315", {"points": [v(-5.1, 16.35) * mm, v(-5.14, 16.39) * mm, v(-5.24, 16.45) * mm, v(-5.41, 16.51) * mm, v(-5.62, 16.54) * mm, v(-5.85, 16.5) * mm, v(-6.04, 16.34) * mm, v(-6.1, 16.12) * mm, v(-6.05, 15.9) * mm, v(-5.85, 15.76) * mm, v(-5.63, 15.7) * mm, v(-5.44, 15.66) * mm, v(-5.31, 15.59) * mm, v(-5.29, 15.48) * mm, v(-5.32, 15.38) * mm, v(-5.42, 15.31) * mm, v(-5.56, 15.3) * mm, v(-5.7, 15.32) * mm, v(-5.86, 15.38) * mm, v(-5.94, 15.45) * mm, v(-5.99, 15.49) * mm]});
            skFitSpline(sketch, "E316", {"points": [v(-6.14, 15.3) * mm, v(-6.08, 15.26) * mm, v(-5.97, 15.18) * mm, v(-5.76, 15.1) * mm, v(-5.53, 15.07) * mm, v(-5.3, 15.1) * mm, v(-5.1, 15.27) * mm, v(-5.03, 15.5) * mm, v(-5.08, 15.71) * mm, v(-5.27, 15.86) * mm, v(-5.49, 15.92) * mm, v(-5.68, 15.96) * mm, v(-5.82, 16.03) * mm, v(-5.83, 16.1) * mm, v(-5.83, 16.14) * mm]});
            skFitSpline(sketch, "E317", {"points": [v(-2.68, 15.8) * mm, v(-2.7, 15.93) * mm, v(-2.74, 16.18) * mm, v(-3.03, 16.47) * mm, v(-3.41, 16.56) * mm, v(-3.8, 16.47) * mm, v(-4.08, 16.18) * mm, v(-4.15, 15.93) * mm, v(-4.15, 15.8) * mm, v(-4.15, 15.8) * mm]});
            skFitSpline(sketch, "E318", {"points": [v(-4.15, 15.8) * mm, v(-4.15, 15.68) * mm, v(-4.09, 15.43) * mm, v(-3.8, 15.14) * mm, v(-3.42, 15.05) * mm, v(-3.03, 15.15) * mm, v(-2.74, 15.43) * mm, v(-2.7, 15.68) * mm, v(-2.68, 15.8) * mm]});
            skFitSpline(sketch, "E319", {"points": [v(-2.94, 15.8) * mm, v(-2.95, 15.72) * mm, v(-2.97, 15.55) * mm, v(-3.16, 15.35) * mm, v(-3.41, 15.28) * mm, v(-3.67, 15.35) * mm, v(-3.85, 15.55) * mm, v(-3.89, 15.72) * mm, v(-3.89, 15.8) * mm]});
            skFitSpline(sketch, "E320", {"points": [v(-3.89, 15.8) * mm, v(-3.89, 15.8) * mm, v(-3.9, 15.9) * mm, v(-3.85, 16.06) * mm, v(-3.67, 16.26) * mm, v(-3.42, 16.33) * mm, v(-3.16, 16.26) * mm, v(-2.98, 16.06) * mm, v(-2.95, 15.9) * mm, v(-2.94, 15.8) * mm]});
            skFitSpline(sketch, "E321", {"points": [v(1.13, 15.8) * mm, v(1.1, 15.93) * mm, v(1.07, 16.18) * mm, v(0.77, 16.46) * mm, v(0.52, 16.5) * mm, v(0.38, 16.5) * mm]});
            skFitSpline(sketch, "E322", {"points": [v(0.38, 15.1) * mm, v(0.52, 15.12) * mm, v(0.77, 15.15) * mm, v(1.07, 15.44) * mm, v(1.1, 15.68) * mm, v(1.13, 15.8) * mm]});
            skFitSpline(sketch, "E323", {"points": [v(0.87, 15.8) * mm, v(0.86, 15.72) * mm, v(0.84, 15.55) * mm, v(0.64, 15.36) * mm, v(0.47, 15.34) * mm, v(0.38, 15.33) * mm]});
            skFitSpline(sketch, "E324", {"points": [v(0.38, 16.28) * mm, v(0.47, 16.27) * mm, v(0.64, 16.25) * mm, v(0.84, 16.06) * mm, v(0.86, 15.89) * mm, v(0.87, 15.8) * mm]});
            skFitSpline(sketch, "E325", {"points": [v(4.53, 15.94) * mm, v(4.59, 15.95) * mm, v(4.7, 15.96) * mm, v(4.83, 16.1) * mm, v(4.83, 16.2) * mm, v(4.84, 16.27) * mm]});
            skFitSpline(sketch, "E326", {"points": [v(4.67, 16.23) * mm, v(4.67, 16.2) * mm, v(4.67, 16.14) * mm, v(4.6, 16.07) * mm, v(4.54, 16.05) * mm, v(4.5, 16.04) * mm]});
            skFitSpline(sketch, "E327", {"points": [v(7.45, 15.7) * mm, v(7.44, 15.63) * mm, v(7.43, 15.49) * mm, v(7.29, 15.33) * mm, v(7.1, 15.3) * mm, v(6.9, 15.33) * mm, v(6.75, 15.5) * mm, v(6.74, 15.63) * mm, v(6.74, 15.7) * mm]});
            skFitSpline(sketch, "E328", {"points": [v(6.5, 15.7) * mm, v(6.5, 15.58) * mm, v(6.52, 15.36) * mm, v(6.77, 15.12) * mm, v(7.09, 15.07) * mm, v(7.41, 15.12) * mm, v(7.66, 15.37) * mm, v(7.68, 15.6) * mm, v(7.7, 15.71) * mm]});
            skFitSpline(sketch, "E329", {"points": [v(9.32, 15.8) * mm, v(9.3, 15.93) * mm, v(9.26, 16.18) * mm, v(8.96, 16.46) * mm, v(8.7, 16.5) * mm, v(8.57, 16.5) * mm]});
            skFitSpline(sketch, "E330", {"points": [v(8.57, 15.1) * mm, v(8.7, 15.12) * mm, v(8.96, 15.15) * mm, v(9.26, 15.44) * mm, v(9.3, 15.68) * mm, v(9.32, 15.8) * mm]});
            skFitSpline(sketch, "E331", {"points": [v(9.06, 15.8) * mm, v(9.05, 15.72) * mm, v(9.03, 15.55) * mm, v(8.83, 15.36) * mm, v(8.66, 15.34) * mm, v(8.57, 15.33) * mm]});
            skFitSpline(sketch, "E332", {"points": [v(8.57, 16.28) * mm, v(8.66, 16.27) * mm, v(8.83, 16.25) * mm, v(9.03, 16.06) * mm, v(9.05, 15.89) * mm, v(9.06, 15.8) * mm]});
            skFitSpline(sketch, "E333", {"points": [v(12.12, 15.49) * mm, v(12.08, 15.46) * mm, v(12, 15.39) * mm, v(11.87, 15.32) * mm, v(11.68, 15.3) * mm, v(11.46, 15.35) * mm, v(11.29, 15.55) * mm, v(11.23, 15.8) * mm, v(11.29, 16.06) * mm, v(11.46, 16.26) * mm, v(11.68, 16.32) * mm, v(11.86, 16.3) * mm, v(12, 16.23) * mm, v(12.07, 16.16) * mm, v(12.1, 16.13) * mm]});
            skFitSpline(sketch, "E334", {"points": [v(12.26, 16.31) * mm, v(12.22, 16.35) * mm, v(12.12, 16.44) * mm, v(11.93, 16.52) * mm, v(11.66, 16.55) * mm, v(11.33, 16.47) * mm, v(11.05, 16.18) * mm, v(10.96, 15.8) * mm, v(11.05, 15.43) * mm, v(11.33, 15.14) * mm, v(11.66, 15.06) * mm, v(11.93, 15.1) * mm, v(12.13, 15.19) * mm, v(12.23, 15.28) * mm, v(12.27, 15.33) * mm]});
            skFitSpline(sketch, "E335", {"points": [v(13.63, 22.17) * mm, v(13.64, 22.28) * mm, v(13.68, 22.53) * mm, v(14.01, 22.78) * mm, v(14.44, 22.85) * mm, v(14.9, 22.78) * mm, v(15.36, 22.58) * mm, v(15.64, 22.37) * mm, v(15.78, 22.26) * mm]});
            skFitSpline(sketch, "E336", {"points": [v(16.25, 23) * mm, v(16.08, 23.13) * mm, v(15.74, 23.4) * mm, v(15.12, 23.64) * mm, v(14.38, 23.73) * mm, v(13.56, 23.57) * mm, v(12.89, 22.95) * mm, v(12.7, 22.1) * mm, v(12.85, 21.23) * mm, v(13.55, 20.66) * mm, v(14.1, 20.5) * mm, v(14.4, 20.42) * mm]});
            skFitSpline(sketch, "E337", {"points": [v(14.4, 20.42) * mm, v(14.64, 20.36) * mm, v(15.02, 20.26) * mm, v(15.47, 19.97) * mm, v(15.56, 19.56) * mm, v(15.46, 19.17) * mm, v(15.1, 18.9) * mm, v(14.61, 18.84) * mm, v(14.07, 18.92) * mm, v(13.53, 19.18) * mm, v(13.23, 19.45) * mm, v(13.08, 19.59) * mm]});
            skFitSpline(sketch, "E338", {"points": [v(12.55, 18.9) * mm, v(12.76, 18.72) * mm, v(13.15, 18.37) * mm, v(13.88, 18.07) * mm, v(14.69, 17.97) * mm, v(15.55, 18.11) * mm, v(16.27, 18.75) * mm, v(16.46, 19.62) * mm, v(16.3, 20.46) * mm, v(15.65, 21.04) * mm, v(15.1, 21.2) * mm, v(14.8, 21.29) * mm]});
            skFitSpline(sketch, "E339", {"points": [v(14.8, 21.29) * mm, v(14.56, 21.35) * mm, v(14.18, 21.46) * mm, v(13.68, 21.75) * mm, v(13.64, 22.03) * mm, v(13.63, 22.17) * mm]});
            skFitSpline(sketch, "E340", {"points": [v(13.63, -27.84) * mm, v(13.64, -27.72) * mm, v(13.68, -27.48) * mm, v(14.01, -27.22) * mm, v(14.44, -27.15) * mm, v(14.9, -27.22) * mm, v(15.36, -27.42) * mm, v(15.64, -27.63) * mm, v(15.78, -27.74) * mm]});
            skFitSpline(sketch, "E341", {"points": [v(16.25, -27) * mm, v(16.08, -26.87) * mm, v(15.74, -26.6) * mm, v(15.12, -26.37) * mm, v(14.38, -26.28) * mm, v(13.56, -26.43) * mm, v(12.89, -27.05) * mm, v(12.7, -27.9) * mm, v(12.85, -28.77) * mm, v(13.55, -29.34) * mm, v(14.1, -29.5) * mm, v(14.4, -29.58) * mm]});
            skFitSpline(sketch, "E342", {"points": [v(14.4, -29.58) * mm, v(14.64, -29.64) * mm, v(15.02, -29.74) * mm, v(15.47, -30.04) * mm, v(15.56, -30.44) * mm, v(15.46, -30.83) * mm, v(15.1, -31.1) * mm, v(14.61, -31.16) * mm, v(14.07, -31.08) * mm, v(13.53, -30.82) * mm, v(13.23, -30.55) * mm, v(13.08, -30.42) * mm]});
            skFitSpline(sketch, "E343", {"points": [v(12.55, -31.11) * mm, v(12.76, -31.29) * mm, v(13.15, -31.63) * mm, v(13.88, -31.93) * mm, v(14.69, -32.04) * mm, v(15.55, -31.9) * mm, v(16.27, -31.25) * mm, v(16.46, -30.38) * mm, v(16.3, -29.54) * mm, v(15.65, -28.96) * mm, v(15.1, -28.8) * mm, v(14.8, -28.71) * mm]});
            skFitSpline(sketch, "E344", {"points": [v(14.8, -28.71) * mm, v(14.56, -28.65) * mm, v(14.18, -28.55) * mm, v(13.68, -28.25) * mm, v(13.64, -27.97) * mm, v(13.63, -27.84) * mm]});
            skSolve(sketch);
        }
        {
            var Q0;
            Q0=makeQuery(id+"F0.imprint","IMPRINT",FACE,{"disambiguationData":[TD([[makeQuery(id+"F0.imprint","IMPRINT",EDGE,{"derivedFrom":sQuery(id+"F0.wireOp",EDGE,"E0")}),1.0]])]});
            var Q1;
            Q1=makeQuery(id+"F0.imprint","IMPRINT",FACE,{"disambiguationData":[TD([[makeQuery(id+"F0.imprint","IMPRINT",EDGE,{"derivedFrom":sQuery(id+"F0.wireOp",EDGE,"E4")}),1.0]])]});
            extrude(context, id + "F1", {"entities" : qUnion([Q0, Q1]), "depth" : 4 * mm, "offsetDistance" : 25 * mm});
        }
        {
            var Q0;
            Q0=makeQuery(id+"F0.imprint","IMPRINT",FACE,{"disambiguationData":[TD([[makeQuery(id+"F0.imprint","IMPRINT",EDGE,{"derivedFrom":sQuery(id+"F0.wireOp",EDGE,"E0")}),1.0]])]});
            var Q1;
            Q1=makeQuery(id+"F0.imprint","IMPRINT",FACE,{"disambiguationData":[TD([[makeQuery(id+"F0.imprint","IMPRINT",EDGE,{"derivedFrom":sQuery(id+"F0.wireOp",EDGE,"E163")}),1.0]])]});
            var Q2;
            Q2=makeQuery(id+"F0.imprint","IMPRINT",FACE,{"disambiguationData":[TD([[makeQuery(id+"F0.imprint","IMPRINT",EDGE,{"derivedFrom":sQuery(id+"F0.wireOp",EDGE,"E175")}),1.0]])]});
            var Q3;
            Q3=makeQuery(id+"F0.imprint","IMPRINT",FACE,{"disambiguationData":[TD([[makeQuery(id+"F0.imprint","IMPRINT",EDGE,{"derivedFrom":sQuery(id+"F0.wireOp",EDGE,"E187")}),1.0]])]});
            var Q4;
            Q4=makeQuery(id+"F0.imprint","IMPRINT",FACE,{"disambiguationData":[TD([[makeQuery(id+"F0.imprint","IMPRINT",EDGE,{"derivedFrom":sQuery(id+"F0.wireOp",EDGE,"E193")}),1.0]])]});
            var Q5;
            Q5=makeQuery(id+"F0.imprint","IMPRINT",FACE,{"disambiguationData":[TD([[makeQuery(id+"F0.imprint","IMPRINT",EDGE,{"derivedFrom":sQuery(id+"F0.wireOp",EDGE,"E205")}),1.0]])]});
            var Q6;
            Q6=makeQuery(id+"F0.imprint","IMPRINT",FACE,{"disambiguationData":[TD([[makeQuery(id+"F0.imprint","IMPRINT",EDGE,{"derivedFrom":sQuery(id+"F0.wireOp",EDGE,"E215")}),1.0]])]});
            var Q7;
            Q7=makeQuery(id+"F0.imprint","IMPRINT",FACE,{"disambiguationData":[TD([[makeQuery(id+"F0.imprint","IMPRINT",EDGE,{"derivedFrom":sQuery(id+"F0.wireOp",EDGE,"E219")}),1.0]])]});
            var Q8;
            Q8=makeQuery(id+"F0.imprint","IMPRINT",FACE,{"disambiguationData":[TD([[makeQuery(id+"F0.imprint","IMPRINT",EDGE,{"derivedFrom":sQuery(id+"F0.wireOp",EDGE,"E139")}),1.0]])]});
            var Q9;
            Q9=makeQuery(id+"F0.imprint","IMPRINT",FACE,{"disambiguationData":[TD([[makeQuery(id+"F0.imprint","IMPRINT",EDGE,{"derivedFrom":sQuery(id+"F0.wireOp",EDGE,"E143")}),1.0]])]});
            var Q10;
            Q10=makeQuery(id+"F0.imprint","IMPRINT",FACE,{"disambiguationData":[TD([[makeQuery(id+"F0.imprint","IMPRINT",EDGE,{"derivedFrom":sQuery(id+"F0.wireOp",EDGE,"E151")}),1.0]])]});
            var Q11;
            Q11=makeQuery(id+"F0.imprint","IMPRINT",FACE,{"disambiguationData":[TD([[makeQuery(id+"F0.imprint","IMPRINT",EDGE,{"derivedFrom":sQuery(id+"F0.wireOp",EDGE,"E159")}),1.0]])]});
            var Q12;
            Q12=makeQuery(id+"F0.imprint","IMPRINT",FACE,{"disambiguationData":[TD([[makeQuery(id+"F0.imprint","IMPRINT",EDGE,{"derivedFrom":sQuery(id+"F0.wireOp",EDGE,"E155")}),1.0]])]});
            var Q13;
            Q13=makeQuery(id+"F0.imprint","IMPRINT",FACE,{"disambiguationData":[TD([[makeQuery(id+"F0.imprint","IMPRINT",EDGE,{"derivedFrom":sQuery(id+"F0.wireOp",EDGE,"E147")}),1.0]])]});
            var Q14;
            Q14=makeQuery(id+"F0.imprint","IMPRINT",FACE,{"disambiguationData":[TD([[makeQuery(id+"F0.imprint","IMPRINT",EDGE,{"derivedFrom":sQuery(id+"F0.wireOp",EDGE,"E8")}),1.0]])]});
            var Q15;
            Q15=makeQuery(id+"F0.imprint","IMPRINT",FACE,{"disambiguationData":[TD([[makeQuery(id+"F0.imprint","IMPRINT",EDGE,{"derivedFrom":sQuery(id+"F0.wireOp",EDGE,"E14")}),1.0]])]});
            var Q16;
            Q16=makeQuery(id+"F0.imprint","IMPRINT",FACE,{"disambiguationData":[TD([[makeQuery(id+"F0.imprint","IMPRINT",EDGE,{"derivedFrom":sQuery(id+"F0.wireOp",EDGE,"E25")}),1.0]])]});
            var Q17;
            Q17=makeQuery(id+"F0.imprint","IMPRINT",FACE,{"disambiguationData":[TD([[makeQuery(id+"F0.imprint","IMPRINT",EDGE,{"derivedFrom":sQuery(id+"F0.wireOp",EDGE,"E33")}),1.0]])]});
            var Q18;
            Q18=makeQuery(id+"F0.imprint","IMPRINT",FACE,{"disambiguationData":[TD([[makeQuery(id+"F0.imprint","IMPRINT",EDGE,{"derivedFrom":sQuery(id+"F0.wireOp",EDGE,"E44")}),1.0]])]});
            var Q19;
            Q19=makeQuery(id+"F0.imprint","IMPRINT",FACE,{"disambiguationData":[TD([[makeQuery(id+"F0.imprint","IMPRINT",EDGE,{"derivedFrom":sQuery(id+"F0.wireOp",EDGE,"E46")}),1.0]])]});
            var Q20;
            Q20=makeQuery(id+"F0.imprint","IMPRINT",FACE,{"disambiguationData":[TD([[makeQuery(id+"F0.imprint","IMPRINT",EDGE,{"derivedFrom":sQuery(id+"F0.wireOp",EDGE,"E48")}),1.0]])]});
            var Q21;
            Q21=makeQuery(id+"F0.imprint","IMPRINT",FACE,{"disambiguationData":[TD([[makeQuery(id+"F0.imprint","IMPRINT",EDGE,{"derivedFrom":sQuery(id+"F0.wireOp",EDGE,"E317")}),1.0]])]});
            var Q22;
            Q22=makeQuery(id+"F0.imprint","IMPRINT",FACE,{"disambiguationData":[TD([[makeQuery(id+"F0.imprint","IMPRINT",EDGE,{"derivedFrom":sQuery(id+"F0.wireOp",EDGE,"E319")}),-1.0]])]});
            var Q23;
            Q23=makeQuery(id+"F0.imprint","IMPRINT",FACE,{"disambiguationData":[TD([[makeQuery(id+"F0.imprint","IMPRINT",EDGE,{"derivedFrom":sQuery(id+"F0.wireOp",EDGE,"E62")}),1.0]])]});
            var Q24;
            Q24=makeQuery(id+"F0.imprint","IMPRINT",FACE,{"disambiguationData":[TD([[makeQuery(id+"F0.imprint","IMPRINT",EDGE,{"derivedFrom":sQuery(id+"F0.wireOp",EDGE,"E68")}),1.0]])]});
            var Q25;
            Q25=makeQuery(id+"F0.imprint","IMPRINT",FACE,{"disambiguationData":[TD([[makeQuery(id+"F0.imprint","IMPRINT",EDGE,{"derivedFrom":sQuery(id+"F0.wireOp",EDGE,"E80")}),1.0]])]});
            var Q26;
            Q26=makeQuery(id+"F0.imprint","IMPRINT",FACE,{"disambiguationData":[TD([[makeQuery(id+"F0.imprint","IMPRINT",EDGE,{"derivedFrom":sQuery(id+"F0.wireOp",EDGE,"E86")}),1.0]])]});
            var Q27;
            Q27=makeQuery(id+"F0.imprint","IMPRINT",FACE,{"disambiguationData":[TD([[makeQuery(id+"F0.imprint","IMPRINT",EDGE,{"derivedFrom":sQuery(id+"F0.wireOp",EDGE,"E91")}),1.0]])]});
            var Q28;
            Q28=makeQuery(id+"F0.imprint","IMPRINT",FACE,{"disambiguationData":[TD([[makeQuery(id+"F0.imprint","IMPRINT",EDGE,{"derivedFrom":sQuery(id+"F0.wireOp",EDGE,"E102")}),1.0]])]});
            var Q29;
            Q29=makeQuery(id+"F0.imprint","IMPRINT",FACE,{"disambiguationData":[TD([[makeQuery(id+"F0.imprint","IMPRINT",EDGE,{"derivedFrom":sQuery(id+"F0.wireOp",EDGE,"E108")}),1.0]])]});
            var Q30;
            Q30=makeQuery(id+"F0.imprint","IMPRINT",FACE,{"disambiguationData":[TD([[makeQuery(id+"F0.imprint","IMPRINT",EDGE,{"derivedFrom":sQuery(id+"F0.wireOp",EDGE,"E127")}),1.0]])]});
            var Q31;
            Q31=makeQuery(id+"F0.imprint","IMPRINT",FACE,{"disambiguationData":[TD([[makeQuery(id+"F0.imprint","IMPRINT",EDGE,{"derivedFrom":sQuery(id+"F0.wireOp",EDGE,"E125")}),1.0]])]});
            var Q32;
            Q32=makeQuery(id+"F0.imprint","IMPRINT",FACE,{"disambiguationData":[TD([[makeQuery(id+"F0.imprint","IMPRINT",EDGE,{"derivedFrom":sQuery(id+"F0.wireOp",EDGE,"E122")}),-1.0]])]});
            var Q33;
            Q33=makeQuery(id+"F0.imprint","IMPRINT",FACE,{"disambiguationData":[TD([[makeQuery(id+"F0.imprint","IMPRINT",EDGE,{"derivedFrom":sQuery(id+"F0.wireOp",EDGE,"E111")}),-1.0]])]});
            var Q34;
            Q34=makeQuery(id+"F0.imprint","IMPRINT",FACE,{"disambiguationData":[TD([[makeQuery(id+"F0.imprint","IMPRINT",EDGE,{"derivedFrom":sQuery(id+"F0.wireOp",EDGE,"E114")}),1.0]])]});
            var Q35;
            Q35=makeQuery(id+"F0.imprint","IMPRINT",FACE,{"disambiguationData":[TD([[makeQuery(id+"F0.imprint","IMPRINT",EDGE,{"derivedFrom":sQuery(id+"F0.wireOp",EDGE,"E52")}),1.0]])]});
            var Q36;
            Q36=makeQuery(id+"F0.imprint","IMPRINT",FACE,{"disambiguationData":[TD([[makeQuery(id+"F0.imprint","IMPRINT",EDGE,{"derivedFrom":sQuery(id+"F0.wireOp",EDGE,"E65")}),-1.0]])]});
            var Q37;
            Q37=makeQuery(id+"F0.imprint","IMPRINT",FACE,{"disambiguationData":[TD([[makeQuery(id+"F0.imprint","IMPRINT",EDGE,{"derivedFrom":sQuery(id+"F0.wireOp",EDGE,"E99")}),-1.0]])]});
            var Q38;
            Q38=makeQuery(id+"F0.imprint","IMPRINT",FACE,{"disambiguationData":[TD([[makeQuery(id+"F0.imprint","IMPRINT",EDGE,{"derivedFrom":sQuery(id+"F0.wireOp",EDGE,"E41")}),-1.0]])]});
            var Q39;
            Q39=makeQuery(id+"F0.imprint","IMPRINT",FACE,{"disambiguationData":[TD([[makeQuery(id+"F0.imprint","IMPRINT",EDGE,{"derivedFrom":sQuery(id+"F0.wireOp",EDGE,"E30")}),-1.0]])]});
            var Q40;
            Q40=makeQuery(id+"F0.imprint","IMPRINT",FACE,{"disambiguationData":[TD([[makeQuery(id+"F0.imprint","IMPRINT",EDGE,{"derivedFrom":sQuery(id+"F0.wireOp",EDGE,"E22")}),-1.0]])]});
            extrude(context, id + "F2", {"entities" : qUnion([Q0, Q1, Q2, Q3, Q4, Q5, Q6, Q7, Q8, Q9, Q10, Q11, Q12, Q13, Q14, Q15, Q16, Q17, Q18, Q19, Q20, Q21, Q22, Q23, Q24, Q25, Q26, Q27, Q28, Q29, Q30, Q31, Q32, Q33, Q34, Q35, Q36, Q37, Q38, Q39, Q40]), "operationType" : NewBodyOperationType.ADD, "depth" : 3.2 * mm, "offsetDistance" : 25 * mm});
        }
        {
            var Q0;
            Q0=makeQuery(id+"F0.imprint","IMPRINT",FACE,{"disambiguationData":[TD([[makeQuery(id+"F0.imprint","IMPRINT",EDGE,{"derivedFrom":sQuery(id+"F0.wireOp",EDGE,"E4")}),1.0]])]});
            var Q1;
            Q1=makeQuery(id+"F0.imprint","IMPRINT",FACE,{"disambiguationData":[TD([[makeQuery(id+"F0.imprint","IMPRINT",EDGE,{"derivedFrom":sQuery(id+"F0.wireOp",EDGE,"E245")}),1.0]])]});
            var Q2;
            Q2=makeQuery(id+"F0.imprint","IMPRINT",FACE,{"disambiguationData":[TD([[makeQuery(id+"F0.imprint","IMPRINT",EDGE,{"derivedFrom":sQuery(id+"F0.wireOp",EDGE,"E257")}),1.0]])]});
            var Q3;
            Q3=makeQuery(id+"F0.imprint","IMPRINT",FACE,{"disambiguationData":[TD([[makeQuery(id+"F0.imprint","IMPRINT",EDGE,{"derivedFrom":sQuery(id+"F0.wireOp",EDGE,"E269")}),1.0]])]});
            var Q4;
            Q4=makeQuery(id+"F0.imprint","IMPRINT",FACE,{"disambiguationData":[TD([[makeQuery(id+"F0.imprint","IMPRINT",EDGE,{"derivedFrom":sQuery(id+"F0.wireOp",EDGE,"E275")}),1.0]])]});
            var Q5;
            Q5=makeQuery(id+"F0.imprint","IMPRINT",FACE,{"disambiguationData":[TD([[makeQuery(id+"F0.imprint","IMPRINT",EDGE,{"derivedFrom":sQuery(id+"F0.wireOp",EDGE,"E287")}),1.0]])]});
            var Q6;
            Q6=makeQuery(id+"F0.imprint","IMPRINT",FACE,{"disambiguationData":[TD([[makeQuery(id+"F0.imprint","IMPRINT",EDGE,{"derivedFrom":sQuery(id+"F0.wireOp",EDGE,"E297")}),1.0]])]});
            var Q7;
            Q7=makeQuery(id+"F0.imprint","IMPRINT",FACE,{"disambiguationData":[TD([[makeQuery(id+"F0.imprint","IMPRINT",EDGE,{"derivedFrom":sQuery(id+"F0.wireOp",EDGE,"E301")}),1.0]])]});
            var Q8;
            Q8=makeQuery(id+"F0.imprint","IMPRINT",FACE,{"disambiguationData":[TD([[makeQuery(id+"F0.imprint","IMPRINT",EDGE,{"derivedFrom":sQuery(id+"F0.wireOp",EDGE,"E221")}),1.0]])]});
            var Q9;
            Q9=makeQuery(id+"F0.imprint","IMPRINT",FACE,{"disambiguationData":[TD([[makeQuery(id+"F0.imprint","IMPRINT",EDGE,{"derivedFrom":sQuery(id+"F0.wireOp",EDGE,"E229")}),1.0]])]});
            var Q10;
            Q10=makeQuery(id+"F0.imprint","IMPRINT",FACE,{"disambiguationData":[TD([[makeQuery(id+"F0.imprint","IMPRINT",EDGE,{"derivedFrom":sQuery(id+"F0.wireOp",EDGE,"E237")}),1.0]])]});
            var Q11;
            Q11=makeQuery(id+"F0.imprint","IMPRINT",FACE,{"disambiguationData":[TD([[makeQuery(id+"F0.imprint","IMPRINT",EDGE,{"derivedFrom":sQuery(id+"F0.wireOp",EDGE,"E241")}),1.0]])]});
            var Q12;
            Q12=makeQuery(id+"F0.imprint","IMPRINT",FACE,{"disambiguationData":[TD([[makeQuery(id+"F0.imprint","IMPRINT",EDGE,{"derivedFrom":sQuery(id+"F0.wireOp",EDGE,"E233")}),1.0]])]});
            var Q13;
            Q13=makeQuery(id+"F0.imprint","IMPRINT",FACE,{"disambiguationData":[TD([[makeQuery(id+"F0.imprint","IMPRINT",EDGE,{"derivedFrom":sQuery(id+"F0.wireOp",EDGE,"E225")}),1.0]])]});
            extrude(context, id + "F3", {"entities" : qUnion([Q0, Q1, Q2, Q3, Q4, Q5, Q6, Q7, Q8, Q9, Q10, Q11, Q12, Q13]), "operationType" : NewBodyOperationType.ADD, "depth" : 3.2 * mm, "offsetDistance" : 25 * mm});
        }
    });
